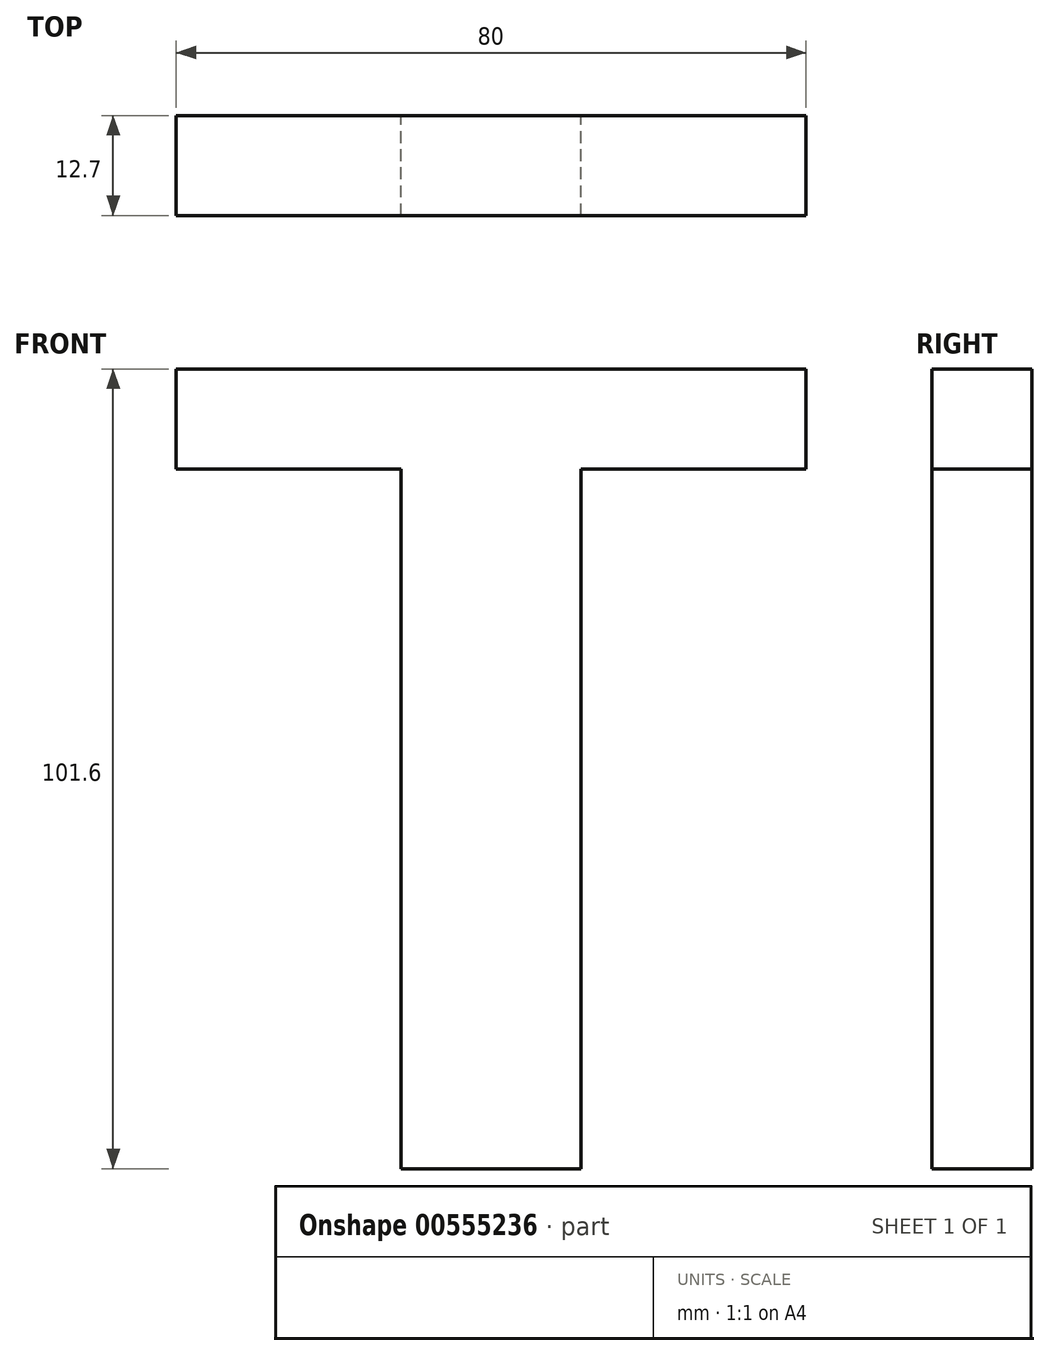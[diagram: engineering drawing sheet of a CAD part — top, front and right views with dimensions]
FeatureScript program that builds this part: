
annotation { "Feature Type Name" : "Feature", "Feature Type Description" : "" }
export const myFeature = defineFeature(function(context is Context, id is Id, definition is map)
    precondition{}
    {
        {
            var Q0;
            Q0=qCreatedBy(makeId("Front.planeOp"),FACE);
            var sketch = newSketch(context, id + "F0", { "sketchPlane" : qUnion([Q0])});
            skLineSegment(sketch, "E0", {"start": v(-38.12, 54.33) * mm, "end": v(-38.12, 41.63) * mm});
            skLineSegment(sketch, "E1", {"start": v(41.88, 41.63) * mm, "end": v(41.88, 54.33) * mm});
            skLineSegment(sketch, "E2", {"start": v(41.88, 54.33) * mm, "end": v(-38.12, 54.33) * mm});
            skLineSegment(sketch, "E3", {"start": v(-38.12, 41.63) * mm, "end": v(-9.55, 41.63) * mm});
            skLineSegment(sketch, "E4", {"start": v(41.88, 41.63) * mm, "end": v(13.3, 41.63) * mm});
            skLineSegment(sketch, "E5", {"start": v(-9.55, 41.63) * mm, "end": v(-9.55, -47.27) * mm});
            skLineSegment(sketch, "E6", {"start": v(13.3, 41.63) * mm, "end": v(13.3, -47.27) * mm});
            skLineSegment(sketch, "E7", {"start": v(13.3, -47.27) * mm, "end": v(-9.55, -47.27) * mm});
            skSolve(sketch);
        }
        {
            var Q0;
            Q0 = qSketchRegion(id + "F0", true);
            extrude(context, id + "F1", {"entities" : qUnion([Q0]), "depth" : 12.7 * mm, "offsetDistance" : 25.4 * mm});
        }
    });
